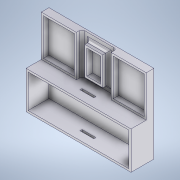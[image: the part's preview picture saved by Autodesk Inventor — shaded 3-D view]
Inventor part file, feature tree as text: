
AUTODESK INVENTOR PART (.ipt)
format: ipt  version: 2021 (Build 250183000, 183)  size: 204,288 bytes
history: native  units: mm
features: extrude x4, sketch x4, fillet x1
ambient origin geometry x8: Origin, YZ Plane, XZ Plane, XY Plane, X Axis, Y Axis, Z Axis, Center Point
bodies: Solid1 (feature_tree)
feature tree (9):
  extrude  "Extrusion1"  Depth=112.0mm
  extrude  "Extrusion2"  Depth=151.0mm
  extrude  "Extrusion3"  Depth=3.0mm
  fillet  "Fillet1"  Radius=3.0mm
  extrude  "Extrusion5"  Depth=3.0mm
  sketch  "Sketch1"  dims[d0=151.0mm d1=112.0mm]
  sketch  "Sketch2"  dims[d2=3.0mm d3=0.0mm d4=151.0mm]
  sketch  "Sketch3"  dims[d5=53.0mm d6=3.0mm d7=3.0mm]
  sketch  "Sketch6"  dims[d8=3.0mm d9=3.0mm d10=30.0mm d11=0.0mm d12=44.5mm d13=53.0mm d14=44.5mm d15=53.0mm d16=3.0mm d17=3.0mm d18=3.0mm d19=20.0mm d20=35.0mm d21=12.0mm d22=18.0mm d23=3.0mm d24=3.0mm d25=3.0mm d26=8.0mm d27=0.0mm d28=4.0mm d35=1.0mm d36=1.0mm d37=20.0mm d38=3.0mm d39=65.5mm d40=12.0mm d41=8.0mm d42=0.0mm]
